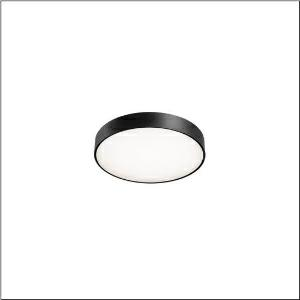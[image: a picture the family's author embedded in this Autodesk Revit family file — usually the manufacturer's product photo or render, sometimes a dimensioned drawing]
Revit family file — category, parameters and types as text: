
# Revit family: round_21_s_51mr34fd0421b
name_source: partatom
category: Lighting Fixtures
units: mm (PartAtom-declared; Revit-internal decimal feet)

## family parameters
Cut with Voids When Loaded = No
Host = Face
Light Source = No
Part Type = Normal
Room Calculation Point = No
Round Connector Dimension = Use Diameter
Shared = No

## types (1)
- Round 21 S (1 x LED, 3910 lm, 30.3 W, 4000K)
    Apparent Load = 30 VA
    CIE Flux Codes = 49 80 96 100 100
    Color Rendering = 80
    Color Temperature = 4000K
    Default Elevation = 1800 mm
    Description = Round 21 S, wall and ceiling luminaire, primary optical cover: cover, of PMMA, opal, light emission: direct distribution, primary light characteristic: symmetric, installation type: suspended mounting, surface-mounted, LED, rated luminous flux: 3.900lm, luminous efficacy: 129lm/W, light colour: 840, colour temperature: 4000K, control gear: DALI 2, with terminal, 5-pole, mains connection: 230V, AC, 50/60Hz, rated input power: 30.3W, housing, of aluminium, coated, black, diameter: 400mm, height: 62mm, protection rating (complete): IP40, insulation class (complete): insulation class I (protective earthing), certification: CE, impact resistance: IK04, permissible operating ambient temperature: -10..+35°C, packaging unit: 1 piece
    Height = 87 mm
    Lamp = 1 x LED
    Lamp Light Flux = 3910 lm
    Lamp Power = 30.3 W
    Lamp count = 1
    Length = 400 mm
    Luminous efficacy = 129 lm/W
    Manufacturer = Siteco
    ModVariant = No
    Model = 51MR34FD0421B
    Mounting Place = Wall
    Mounting Type = Surface mounted
    Number of Poles = 1
    OnlyDefault = Yes
    Power Factor = 1
    Product Name = Round 21 S
    Product group = wall and ceiling luminaire
    ProductGroupID = 2001
    Protection Class = Protection class I
    Protection Degree = IP 40
    RLX_Detail_Level = 1
    RLX_Emergency_Light_Flux = 0 lm
    RLX_Emergency_Type = 0
    RLX_Emergency_Type_DB = No
    RlxData = <blob elided: 13453 chars, md5=95fee971>
    Socket = socket
    Standby Power = 0 W
    System Light Flux = 3910 lm
    System Power = 30 W
    Type Comments = Product without accessories
    Type Image = l_1258311.jpg
    URL = http://relux.com
    VarID = ---
    Voltage = 0 V
    Weight = 0.00 kg
    Width = 0 mm  [stored 0 ft]

note: [stored X ft] marks values corroborated as IEEE doubles in the binary element streams (Revit-internal decimal feet)

## geometry (parser evidence)
native form markers: Sweep x11
no freeform markers — native parametric forms only
